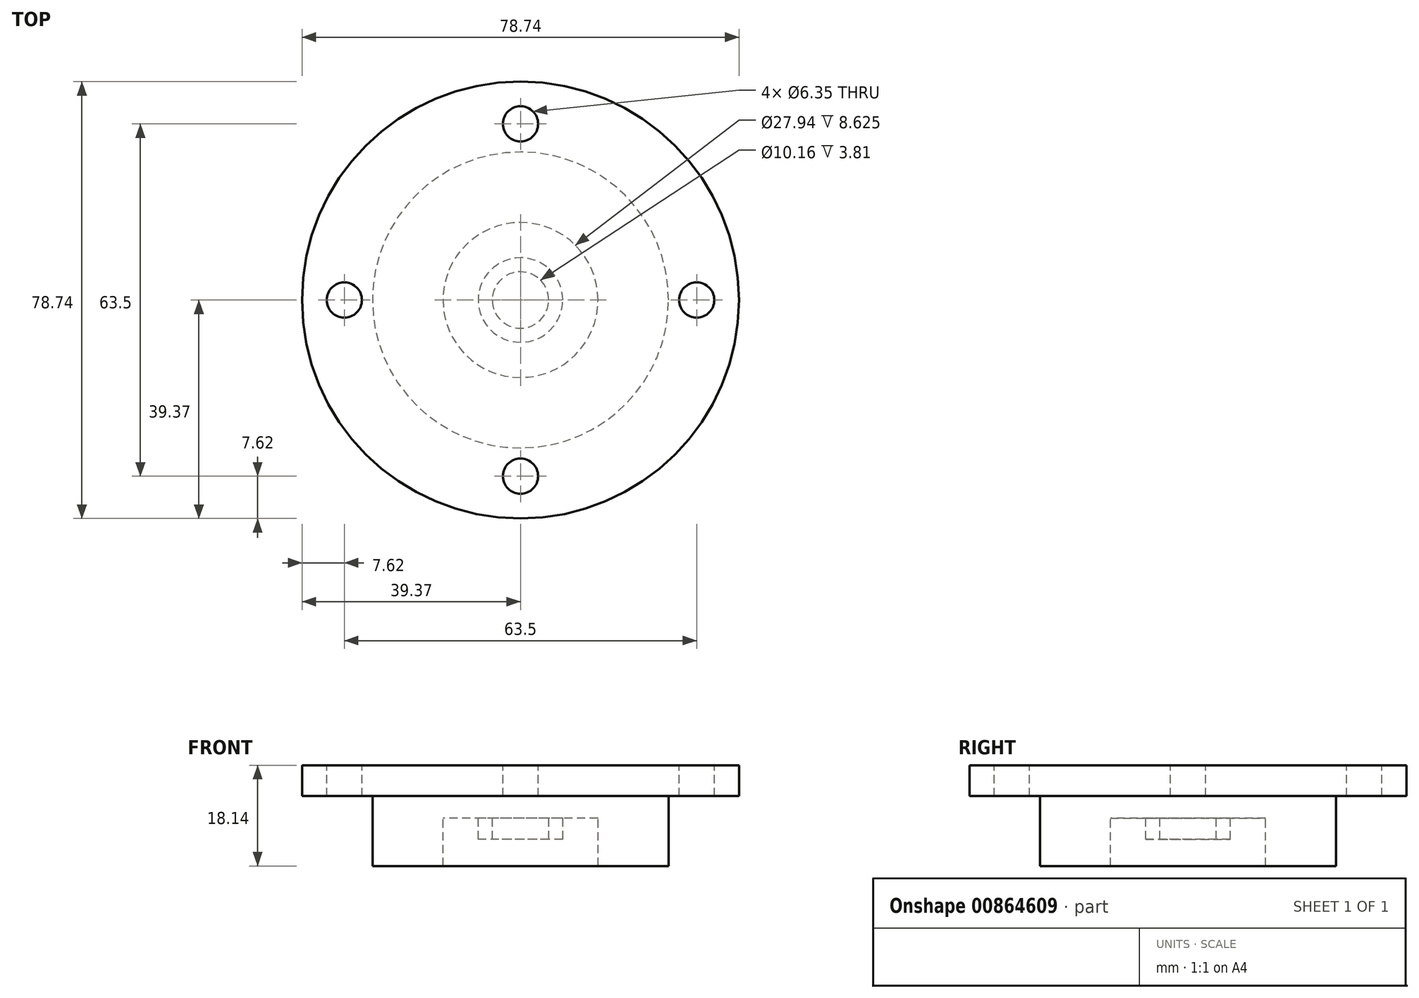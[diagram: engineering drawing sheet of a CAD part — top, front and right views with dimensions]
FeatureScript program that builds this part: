
annotation { "Feature Type Name" : "Feature", "Feature Type Description" : "" }
export const myFeature = defineFeature(function(context is Context, id is Id, definition is map)
    precondition{}
    {
        {
            var Q0;
            Q0=qCreatedBy(makeId("Front.planeOp"),FACE);
            var sketch = newSketch(context, id + "F0", { "sketchPlane" : qUnion([Q0])});
            skLineSegment(sketch, "E0", {"start": v(0, 34.57) * mm, "end": v(0, 8.63) * mm, "construction": true});
            skLineSegment(sketch, "E1", {"start": v(0, 18.14) * mm, "end": v(-39.37, 18.14) * mm});
            skLineSegment(sketch, "E2", {"start": v(-39.37, 18.14) * mm, "end": v(-39.37, 12.6) * mm});
            skLineSegment(sketch, "E3", {"start": v(-39.37, 12.6) * mm, "end": v(-26.67, 12.6) * mm});
            skLineSegment(sketch, "E4", {"start": v(-26.67, 12.6) * mm, "end": v(-26.67, 4.94) * mm});
            skLineSegment(sketch, "E5", {"start": v(-26.67, 0) * mm, "end": v(-13.97, 0) * mm});
            skLineSegment(sketch, "E6", {"start": v(0, 8.63) * mm, "end": v(0, 18.14) * mm});
            skLineSegment(sketch, "E7", {"start": v(-13.97, 0) * mm, "end": v(-13.97, 8.63) * mm});
            skLineSegment(sketch, "E8", {"start": v(-13.97, 8.63) * mm, "end": v(-7.62, 8.63) * mm});
            skLineSegment(sketch, "E9", {"start": v(-7.62, 8.63) * mm, "end": v(-7.62, 4.82) * mm});
            skLineSegment(sketch, "E10", {"start": v(-7.62, 4.82) * mm, "end": v(-5.08, 4.82) * mm});
            skLineSegment(sketch, "E11", {"start": v(-5.08, 4.82) * mm, "end": v(-5.08, 8.63) * mm});
            skLineSegment(sketch, "E12.trimOffspring", {"start": v(-5.08, 8.63) * mm, "end": v(0, 8.63) * mm});
            skLineSegment(sketch, "E13.trimOffspring", {"start": v(0, 4.82) * mm, "end": v(0, -36.08) * mm, "construction": true});
            skLineSegment(sketch, "E14", {"start": v(-13.97, 0) * mm, "end": v(-13.97, -23.48) * mm, "construction": true});
            skLineSegment(sketch, "E15", {"start": v(-13.97, -20.03) * mm, "end": v(0, -20.03) * mm, "construction": true});
            skLineSegment(sketch, "E16", {"start": v(-5.08, 4.82) * mm, "end": v(-5.08, -31.77) * mm, "construction": true});
            skCircle(sketch, "E17", {"center": v(0, -6.82) * mm, "radius": 12.7 * mm, "construction": true});
            skPoint(sketch, "E17.second.point", {"position": v(8.38, -16.37) * mm});
            skPoint(sketch, "E17.third.point", {"position": v(-1.35, -19.45) * mm});
            skPoint(sketch, "E18", {"position": v(-5.08, -20.03) * mm});
            skLineSegment(sketch, "E19", {"start": v(-5.08, -18.46) * mm, "end": v(-21.05, -18.46) * mm, "construction": true});
            skLineSegment(sketch, "E20", {"start": v(-26.67, 4.94) * mm, "end": v(-26.67, 0) * mm});
            skPoint(sketch, "E21.orphan", {"position": v(-29.94, 0) * mm});
            skSolve(sketch);
        }
        {
            var Q0;
            Q0 = qSketchRegion(id + "F0", true);
            var Q1;
            Q1=sQuery(id+"F0.wireOp",EDGE,"E0");
            revolve(context, id + "F1", {"surfaceOperationType" : NewSurfaceOperationType.NEW, "entities" : qUnion([Q0]), "axis" : qUnion([Q1]), "revolveType" : RevolveType.FULL});
        }
        {
            var Q0;
            Q0=makeQuery(id+"F1.opRevolve","SWEPT_FACE",FACE,{"disambiguationData":[OSD([sQuery(id+"F0.wireOp",EDGE,"E1")])]});
            var sketch = newSketch(context, id + "F2", { "sketchPlane" : qUnion([Q0])});
            skCircle(sketch, "E22", {"center": v(0, 0) * mm, "radius": 31.75 * mm, "construction": true});
            skCircle(sketch, "E23", {"center": v(0, 31.75) * mm, "radius": 3.18 * mm});
            skCircle(sketch, "E24", {"center": v(31.75, 0) * mm, "radius": 3.18 * mm});
            skCircle(sketch, "E25", {"center": v(0, -31.75) * mm, "radius": 3.18 * mm});
            skCircle(sketch, "E26", {"center": v(-31.75, 0) * mm, "radius": 3.18 * mm});
            skSolve(sketch);
        }
        {
            var Q0;
            Q0 = qSketchRegion(id + "F2", true);
            extrude(context, id + "F3", {"entities" : qUnion([Q0]), "operationType" : NewBodyOperationType.REMOVE, "endBound" : BoundingType.UP_TO_NEXT, "oppositeDirection" : true, "depth" : 25.4 * mm, "offsetDistance" : 25.4 * mm});
        }
    });
